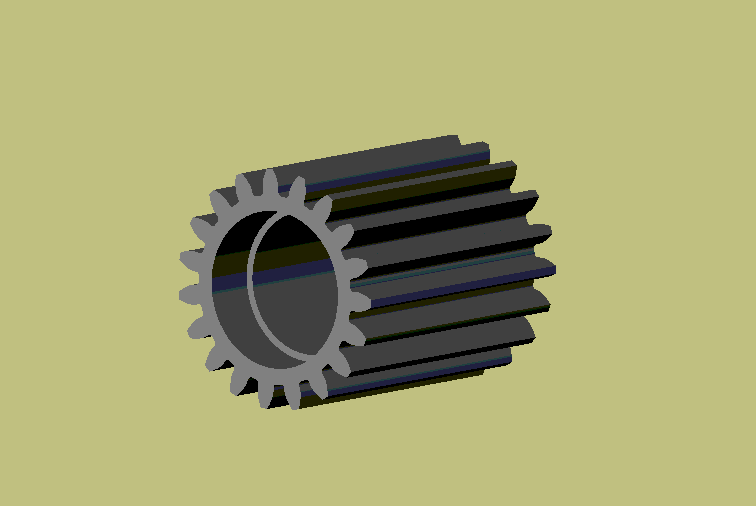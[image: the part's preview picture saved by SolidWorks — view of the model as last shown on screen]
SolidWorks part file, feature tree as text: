
SOLIDWORKS PART (.sldprt)
format: sldprt  version: not decoded by parser v0  size: 400,896 bytes
history: native  units: mm
features: sketch x21, plane x4, cut_extrude x3, material x1, fillet x1, pattern_circular x1 + 1 further entry (+9 scaffold rows collapsed)
feature tree (41):
  scaffold x9  (default folders/planes/origin — collapsed)
  material  "Matériau <non spécifié>"
  plane  "Plane1"
  plane  "Plane2"
  plane  "Plane3"
  "Famille de pièces"
  sketch  "Esquisse1"  dims[c1.D2=7.6mm c1.D1=42.0mm c2.D1=~9.473684deg]
  sketch  "Esquisse2"  dims[c1.D2=~7.447221mm c1.D1=37.0mm c2.D1=~10.243359deg]
  sketch  "Esquisse3"  dims[c1.D2=~7.294443mm c1.D1=33.0mm c2.D1=~10.846766deg]
  sketch  "Esquisse4"  dims[c1.D2=~7.141664mm c1.D1=30.0mm c2.D1=~11.181601deg]
  sketch  "Esquisse5"  dims[c1.D2=~7.866667mm c1.D1=46.0mm c2.D1=~7.836433deg]
  sketch  "Esquisse6"  dims[c1.D2=~8.133333mm c1.D1=50.0mm c2.D1=~5.91069deg]
  sketch  "Esquisse7"  dims[c1.D2=8.4mm c1.D1=54.0mm c2.D1=~3.757333deg]
  plane  "Plan1"  Offset=21mm
  sketch  "Esquisse8"  dims[c1.D2=7.6mm c1.D1=18.0mm c2.D1=~9.473684deg]
  sketch  "Esquisse9"  dims[c1.D2=~7.447221mm c1.D1=15.0mm c2.D1=~10.243359deg]
  sketch  "Esquisse10"  dims[c1.D2=~7.294443mm c1.D1=13.0mm c2.D1=~10.846766deg]
  sketch  "Esquisse11"  dims[c1.D2=~7.141664mm c1.D1=12.0mm c2.D1=~11.181601deg]
  sketch  "Esquisse12"  dims[c1.D2=~7.866667mm c1.D1=20.0mm c2.D1=~7.836433deg]
  sketch  "Esquisse13"  dims[c1.D2=~8.133333mm c1.D1=21.0mm c2.D1=~5.91069deg]
  sketch  "Esquisse14"  dims[c1.D2=8.4mm c1.D1=22.0mm c2.D1=~3.757333deg]
  sketch  "Esquisse15"  dims[c1.D2=6.6mm c1.D1=23.0mm c2.D1=~11.181601deg]
  sketch  "Esquisse16"  dims[c1.D2=6.6mm c1.D1=10.0mm c2.D1=~11.181601deg]
  sketch  "Esquisse17"  dims[D1=13.2mm]
  sketch  "Esquisse18"  dims[D1=13.2mm]
  fillet  "Congé1"  Radius=0.25mm
  pattern_circular  "Répétition circulaire1"  Count=19 Angle=360deg
  sketch  "Esquisse19"  dims[D1=10.0mm]
  cut_extrude  "Enlèv. mat.-Extru.1"  [1 undecoded]
  sketch  "Esquisse20"  dims[D1=11.0mm]
  cut_extrude  "Enlèv. mat.-Extru.2"  Depth=4mm
  sketch  "Esquisse21"  dims[D1=11.0mm]
  cut_extrude  "Enlèv. mat.-Extru.3"  Depth=4mm
decode coverage: 25 of 26 modeling features carry decoded parameters; 1 rows unclassified (native names shown)
note: ~ marks probable driven/reference dimensions
note: 1 parameter value undecoded
note: suppression state not decoded; provenance and decode notes live in map.json
